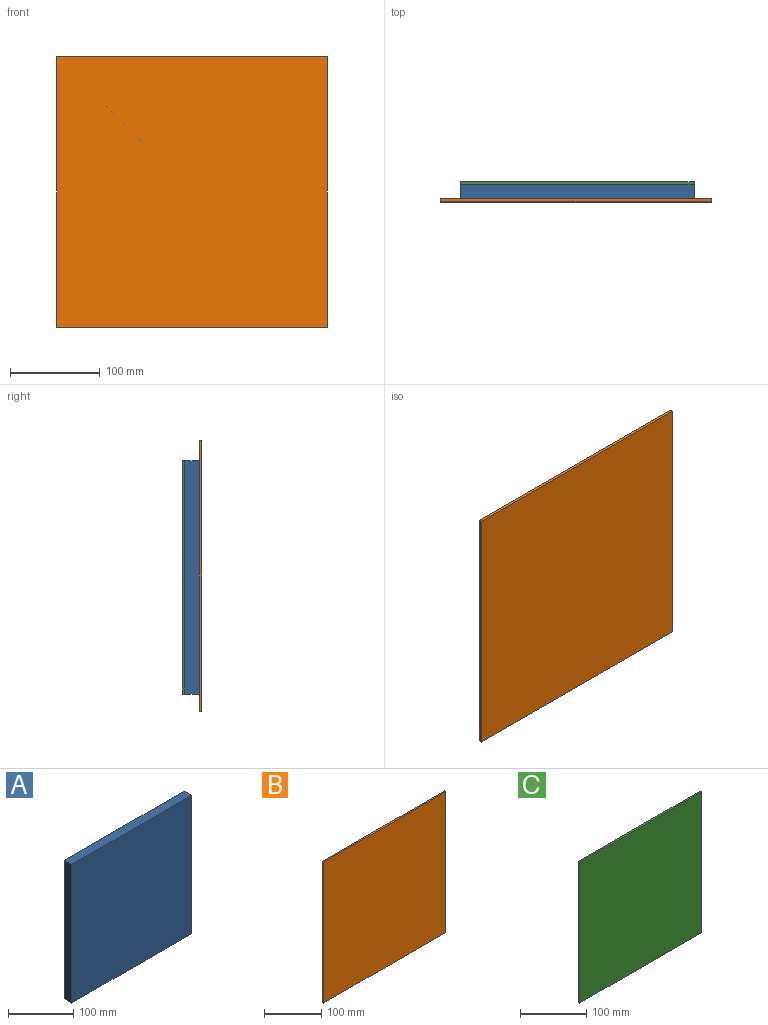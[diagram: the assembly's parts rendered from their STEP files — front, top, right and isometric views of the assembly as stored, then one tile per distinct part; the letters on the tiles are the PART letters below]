
ASSEMBLY  parts=3 mates=2
PART A: 6 faces, bbox 260.4x15.9x260.4 mm
  f0: plane 260.35x15.88mm, normal (1,0,0), area 4133.1mm2, adj f1,f3,f4,f5
  f1: plane 260.35x15.88mm, normal (0,0,1), area 4133.1mm2, adj f0,f2,f4,f5
  f2: plane 260.35x15.88mm, normal (-1,0,0), area 4133.1mm2, adj f1,f3,f4,f5
  f3: plane 260.35x15.88mm, normal (0,0,-1), area 4133.1mm2, adj f0,f2,f4,f5
  f4: plane 260.35x260.35mm, normal (0,-1,0), area 67782.1mm2, adj f0,f1,f2,f3
  f5: plane 260.35x260.35mm, normal (0,1,0), area 67782.1mm2, adj f0,f1,f2,f3
PART B: 6 faces, bbox 301.6x3.2x301.6 mm
  f0: plane 301.63x3.18mm, normal (1,0,0), area 957.7mm2, adj f1,f3,f4,f5
  f1: plane 301.63x3.18mm, normal (0,0,1), area 957.7mm2, adj f0,f2,f4,f5
  f2: plane 301.63x3.18mm, normal (-1,0,0), area 957.7mm2, adj f1,f3,f4,f5
  f3: plane 301.63x3.18mm, normal (0,0,-1), area 957.7mm2, adj f0,f2,f4,f5
  f4: plane 301.63x301.63mm, normal (0,-1,0), area 90977.6mm2, adj f0,f1,f2,f3
  f5: plane 301.63x301.63mm, normal (0,1,0), area 90977.6mm2, adj f0,f1,f2,f3
PART C: 6 faces, bbox 260.4x3.2x260.4 mm
  f0: plane 260.35x3.18mm, normal (1,0,0), area 826.6mm2, adj f1,f3,f4,f5
  f1: plane 260.35x3.18mm, normal (0,0,1), area 826.6mm2, adj f0,f2,f4,f5
  f2: plane 260.35x3.18mm, normal (-1,0,0), area 826.6mm2, adj f1,f3,f4,f5
  f3: plane 260.35x3.18mm, normal (0,0,-1), area 826.6mm2, adj f0,f2,f4,f5
  f4: plane 260.35x260.35mm, normal (0,-1,0), area 67782.1mm2, adj f0,f1,f2,f3
  f5: plane 260.35x260.35mm, normal (0,1,0), area 67782.1mm2, adj f0,f1,f2,f3
PLACE A t=(138.03,-21.38,249.27)mm
PLACE B t=(136.45,-37.26,250.86)mm
PLACE C t=(138.03,-18.21,249.27)mm
MATE fastened A.f4 <-> B.f5  axis (0,-1,0) through (-355.36,-37.26,249.27)mm
MATE fastened C.f4 <-> A.f5  axis (0,-1,0) through (-355.36,-21.38,249.27)mm
